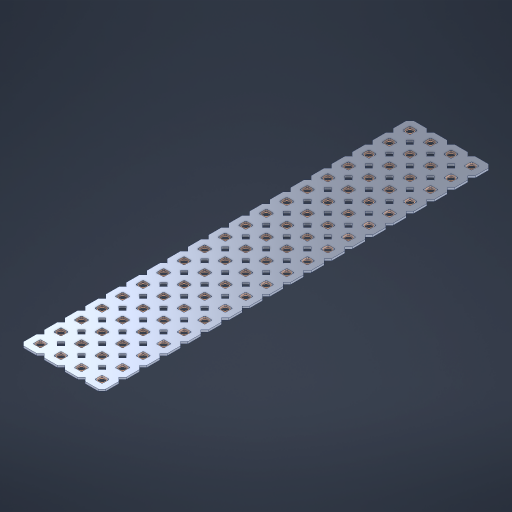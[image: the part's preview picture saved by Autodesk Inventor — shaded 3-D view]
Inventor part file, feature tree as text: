
AUTODESK INVENTOR PART (.ipt)
format: ipt  version: 2023 (Build 270158000, 158)  size: 1,140,224 bytes
history: native  units: in
note: dims shown in document units (in); Inventor stores cm internally (conversion verified against a paired STEP export)
features: other x77, extrude x75, sketch x2, pattern_linear x1
ambient origin geometry x8: Origin, YZ Plane, XZ Plane, XY Plane, X Axis, Y Axis, Z Axis, Center Point
bodies: Solid1 (feature_tree), Body (feature_tree)
feature tree (155):
  pattern_linear  "Rectangular Pattern1"  Spacing1=0.09in  [1 undecoded]
  sketch  "Sketch1"  dims[d1=0.5in]
  sketch  "Sketch2"  dims[d2=0.182in d3=0.09in d4=0.09in d5=0.09in d6=0.09in d7=0.09in d8=0.09in d9=0.09in d10=0.09in d11=0.02in d13=0.0in d14=0.172in d15=0.0625in d16=0.0in d19=0.5in d22=0.5in]
  other  "Srf1"
  other  "Srf126"
  other  "Srf127"
  other  "Srf128"
  other  "Srf129"
  other  "Srf130"
  other  "Srf131"
  other  "Srf250"
  other  "Srf251"
  other  "Srf252"
  other  "Srf253"
  other  "Srf254"
  other  "Srf255"
  other  "Srf256"
  other  "Srf257"
  other  "Srf258"
  other  "Srf259"
  other  "Srf260"
  other  "Srf261"
  other  "Srf268"
  other  "Srf269"
  other  "Srf270"
  other  "Srf271"
  other  "Srf272"
  other  "Srf273"
  other  "Srf274"
  other  "Srf275"
  other  "Srf276"
  other  "Srf277"
  other  "Srf278"
  other  "Srf279"
  other  "Srf280"
  other  "Srf281"
  other  "Srf282"
  other  "Srf283"
  other  "Srf284"
  other  "Srf285"
  other  "Srf286"
  other  "Srf293"
  other  "Srf294"
  other  "Srf295"
  other  "Srf296"
  other  "Srf297"
  other  "Srf298"
  other  "Srf299"
  other  "Srf300"
  other  "Srf301"
  other  "Srf302"
  other  "Srf303"
  other  "Srf304"
  other  "Srf305"
  other  "Srf306"
  other  "Srf307"
  other  "Srf308"
  other  "Srf309"
  other  "Srf310"
  other  "Srf311"
  other  "Srf318"
  other  "Srf319"
  other  "Srf320"
  other  "Srf321"
  other  "Srf322"
  other  "Srf323"
  other  "Srf324"
  other  "Srf325"
  other  "Srf326"
  other  "Srf327"
  other  "Srf328"
  other  "Srf329"
  other  "Srf330"
  other  "Srf331"
  other  "Srf332"
  other  "Srf333"
  other  "Srf334"
  other  "Srf335"
  other  "Srf336"
  other  "Circle"
  extrude  "ExtrusionSrf126"  Depth=0.09in
  extrude  "ExtrusionSrf127"  Depth=0.09in
  extrude  "ExtrusionSrf128"  Depth=0.09in
  extrude  "ExtrusionSrf129"  Depth=0.09in
  extrude  "ExtrusionSrf130"  Depth=0.09in
  extrude  "ExtrusionSrf131"  Depth=0.09in
  extrude  "ExtrusionSrf250"  Depth=0.09in
  extrude  "ExtrusionSrf251"  Depth=0.02in
  extrude  "ExtrusionSrf252"  TaperAngle=0.0deg  [1 undecoded]
  extrude  "ExtrusionSrf253"  Depth=0.5in
  extrude  "ExtrusionSrf254"  Depth=0.5in TaperAngle=0.0deg
  extrude  "ExtrusionSrf255"  Depth=0.5in
  extrude  "ExtrusionSrf256"  Depth=0.5in
  extrude  "ExtrusionSrf257"  [1 undecoded]
  extrude  "ExtrusionSrf258"  [1 undecoded]
  extrude  "ExtrusionSrf259"  [1 undecoded]
  extrude  "ExtrusionSrf260"  [1 undecoded]
  extrude  "ExtrusionSrf261"  [1 undecoded]
  extrude  "ExtrusionSrf268"  [1 undecoded]
  extrude  "ExtrusionSrf269"  [1 undecoded]
  extrude  "ExtrusionSrf270"  [1 undecoded]
  extrude  "ExtrusionSrf271"  [1 undecoded]
  extrude  "ExtrusionSrf272"  [1 undecoded]
  extrude  "ExtrusionSrf273"  [1 undecoded]
  extrude  "ExtrusionSrf274"  [1 undecoded]
  extrude  "ExtrusionSrf275"  [1 undecoded]
  extrude  "ExtrusionSrf276"  [1 undecoded]
  extrude  "ExtrusionSrf277"  [1 undecoded]
  extrude  "ExtrusionSrf278"  [1 undecoded]
  extrude  "ExtrusionSrf279"  [1 undecoded]
  extrude  "ExtrusionSrf280"  [1 undecoded]
  extrude  "ExtrusionSrf281"  [1 undecoded]
  extrude  "ExtrusionSrf282"  [1 undecoded]
  extrude  "ExtrusionSrf283"  [1 undecoded]
  extrude  "ExtrusionSrf284"  [1 undecoded]
  extrude  "ExtrusionSrf285"  [1 undecoded]
  extrude  "ExtrusionSrf286"  [1 undecoded]
  extrude  "ExtrusionSrf293"  [1 undecoded]
  extrude  "ExtrusionSrf294"  [1 undecoded]
  extrude  "ExtrusionSrf295"  [1 undecoded]
  extrude  "ExtrusionSrf296"  [1 undecoded]
  extrude  "ExtrusionSrf297"  [1 undecoded]
  extrude  "ExtrusionSrf298"  [1 undecoded]
  extrude  "ExtrusionSrf299"  [1 undecoded]
  extrude  "ExtrusionSrf300"  [1 undecoded]
  extrude  "ExtrusionSrf301"  [1 undecoded]
  extrude  "ExtrusionSrf302"  [1 undecoded]
  extrude  "ExtrusionSrf303"  [1 undecoded]
  extrude  "ExtrusionSrf304"  [1 undecoded]
  extrude  "ExtrusionSrf305"  [1 undecoded]
  extrude  "ExtrusionSrf306"  [1 undecoded]
  extrude  "ExtrusionSrf307"  [1 undecoded]
  extrude  "ExtrusionSrf308"  [1 undecoded]
  extrude  "ExtrusionSrf309"  [1 undecoded]
  extrude  "ExtrusionSrf310"  [1 undecoded]
  extrude  "ExtrusionSrf311"  [1 undecoded]
  extrude  "ExtrusionSrf318"  [1 undecoded]
  extrude  "ExtrusionSrf319"  [1 undecoded]
  extrude  "ExtrusionSrf320"  [1 undecoded]
  extrude  "ExtrusionSrf321"  [1 undecoded]
  extrude  "ExtrusionSrf322"  [1 undecoded]
  extrude  "ExtrusionSrf323"  [1 undecoded]
  extrude  "ExtrusionSrf324"  [1 undecoded]
  extrude  "ExtrusionSrf325"  [1 undecoded]
  extrude  "ExtrusionSrf326"  [1 undecoded]
  extrude  "ExtrusionSrf327"  [1 undecoded]
  extrude  "ExtrusionSrf328"  [1 undecoded]
  extrude  "ExtrusionSrf329"  [1 undecoded]
  extrude  "ExtrusionSrf330"  [1 undecoded]
  extrude  "ExtrusionSrf331"  [1 undecoded]
  extrude  "ExtrusionSrf332"  [1 undecoded]
  extrude  "ExtrusionSrf333"  [1 undecoded]
  extrude  "ExtrusionSrf334"  [1 undecoded]
  extrude  "ExtrusionSrf335"  [1 undecoded]
  extrude  "ExtrusionSrf336"  [1 undecoded]
note: 64 required parameter values undecoded (feature->parameter linkage not recoverable at this tier; creation-order binding heuristic only, values carry confidence <= 0.55)
